# Revit family: PlumbingFixture_GroheLimited_LineareBasinMixer_23791001_METRIC1
name_source: partatom
category: Plumbing Fixtures
revit_build: Autodesk Revit 2015 (Build: 20160512_1515(x64)
units: mm (PartAtom-declared; Revit-internal decimal feet)

## types (1)
- 23791001
    ADACompliant = No
    Assembly Code = D2010
    AssetType = Fixed
    BIMObjectName = PlumbingFixture_GroheLimited_LineareBasinMixer_23791001_METRIC
    CW Connection = Yes
    CWFU = 4.5
    ClassificationName = Uniclass2015
    ClassificationValue = Pr_40_20_87_82
    ColdWaterConnectionDiameter = 10 mm  [stored 0.0328084 ft]
    Color = Silver
    Cost = 0 $
    Default Elevation = 0 mm  [stored 0 ft]
    Description = Lineare. Basin mixer 1/2". XS-Size. monobloc installation.metal lever. 28 mm ceramic cartridge. with GROHE SilkMove. with temperature limiter. GROHE StarLight chrome finish. GROHE EcoJoy SpeedClean mousseur 5.7 l/min. GROHE QuickFix Plus installation system. smooth body with push-open pop-up waste set 1 1/4". flexible connection hoses.
    DurationUnit = Years
    Ecojoy = No
    ExpectedLife = 0
    Features = Lineare. Basin mixer 1/2". XS-Size. monobloc installation.metal lever. 28 mm ceramic cartridge. with GROHE SilkMove. with temperature limiter. GROHE StarLight chrome finish. GROHE EcoJoy SpeedClean mousseur 5.7 l/min. GROHE QuickFix Plus installation system. smooth body with push-open pop-up waste set 1 1/4". flexible connection hoses.
    Finish = Chrome
    HW Connection = Yes
    HWFU = 4.5
    HotWaterConnectionDiameter = 10 mm  [stored 0.0328084 ft]
    IfcExportAs = IfcPipeFitting
    IfcExportType = IfcPipeFittingType
    Keynote = N13
    LowEmittingMaterial = No
    Manufacturer = Grohe Limited
    ManufacturerName = Grohe Limited
    MasterformatNumber = 01 52 19
    MasterformatTitle = Sanitary Facilities
    Material = Chrome
    Model = Lineare Basin mixer 1/2"XS - Size
    ModelNumber = 23791001
    ModelReference = Lineare Basin mixer 1/2"XS - Size
    NBSDescription = Water supply fittings for sinks
    NBSObjectName = Grohe Limited - Water supply fittings for sinks
    NBSReference = 45-35-70/345
    NominalDepth = 0 mm  [stored 0 ft]
    NominalHeight = 0 mm  [stored 0 ft]
    NominalLength = 0 mm  [stored 0 ft]
    PipeMaterial = GroheLimited-Pipework
    PrimaryMaterial = GroheLimited-Chrome
    ProductDocumentationLink = https://www.grohe.co.uk
    ProductPageURL = https://www.grohe.co.uk
    ProductionYear = 2017
    Type Comments = 23791001
    TypeName = Lineare Basin mixer 1/2"XS - Size
    URL = www.grohe.com
    Vent Connection = No
    WFU = 0
    WarrantyDurationUnit = Years
    Waste Connection = No
    _BSBibleVersion = 14
    _BimSpecGuid = 0
    _CurrentRevision = 1
    _DistributedBy = www.bimstore.co.uk

note: [stored X ft] marks values corroborated as IEEE doubles in the binary element streams (Revit-internal decimal feet)

## geometry (parser evidence)
native form markers: Sweep x1
no freeform markers — native parametric forms only
